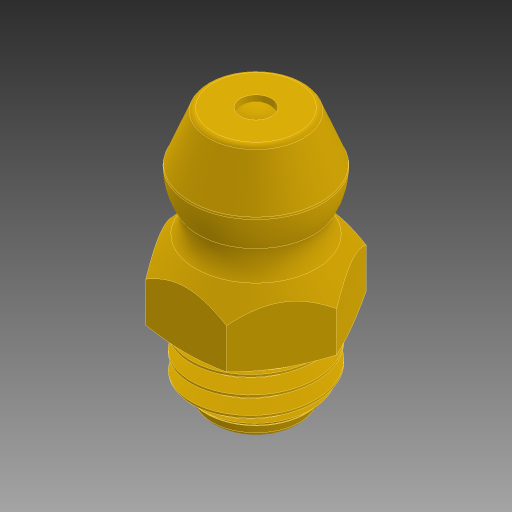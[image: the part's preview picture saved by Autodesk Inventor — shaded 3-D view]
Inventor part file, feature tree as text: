
AUTODESK INVENTOR PART (.ipt)
format: ipt  version: 2023.4 (Build 274418000, 418)  size: 357,888 bytes
history: native  units: in
note: dims shown in document units (in); Inventor stores cm internally (conversion verified against a paired STEP export)
features: other x2, revolve x1
ambient origin geometry x8: Origin, YZ Plane, XZ Plane, XY Plane, X Axis, Y Axis, Z Axis, Center Point
bodies: Solid1 (feature_tree), Solid2 (feature_tree), Solid3 (feature_tree)
feature tree (3):
  revolve  "Revolve4"  [1 undecoded]
  other  "Boss-Extrude4"
  other  "Split3[2]"
note: 1 required parameter value undecoded (feature->parameter linkage not recoverable at this tier; creation-order binding heuristic only, values carry confidence <= 0.55)
